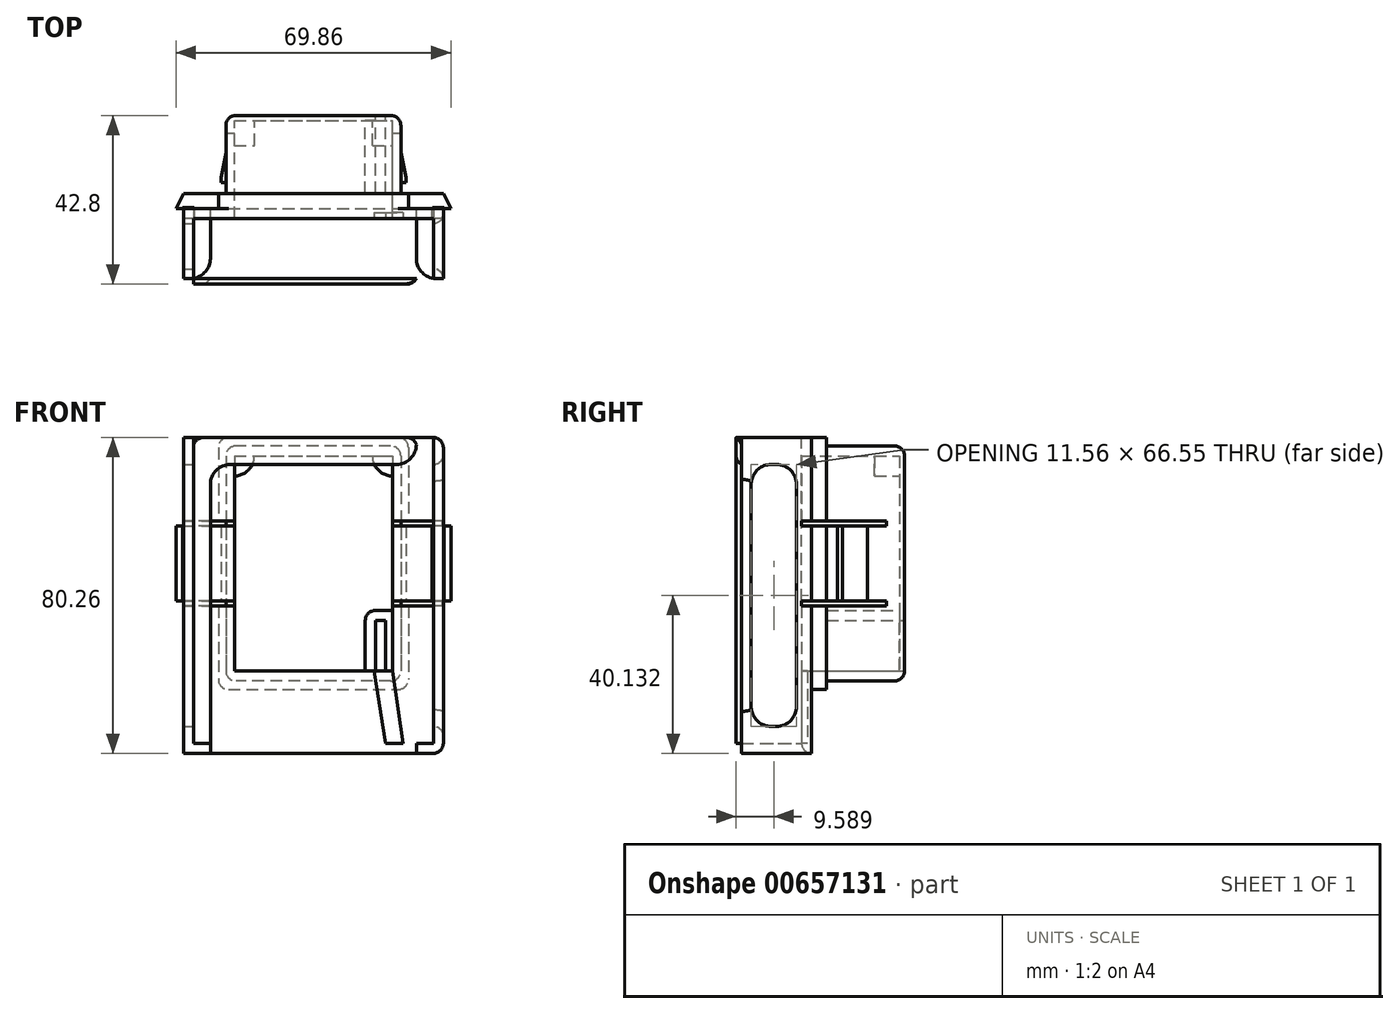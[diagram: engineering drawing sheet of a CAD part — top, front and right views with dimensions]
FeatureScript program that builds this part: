
annotation { "Feature Type Name" : "Feature", "Feature Type Description" : "" }
export const myFeature = defineFeature(function(context is Context, id is Id, definition is map)
    precondition{}
    {
        {
            var Q0;
            Q0=qCreatedBy(makeId("Front.planeOp"),FACE);
            var sketch = newSketch(context, id + "F0", { "sketchPlane" : qUnion([Q0])});
            skLineSegment(sketch, "E0.bottom", {"start": v(22.23, 29.85) * mm, "end": v(-22.23, 29.85) * mm});
            skLineSegment(sketch, "E0.top", {"start": v(22.22, -29.85) * mm, "end": v(-22.23, -29.85) * mm});
            skLineSegment(sketch, "E0.left", {"start": v(22.23, 29.84) * mm, "end": v(22.22, -29.85) * mm});
            skLineSegment(sketch, "E0.right", {"start": v(-22.23, 29.85) * mm, "end": v(-22.23, -29.85) * mm});
            skPoint(sketch, "E0.middle", {"position": v(0, 0) * mm});
            skLineSegment(sketch, "E1.bottom", {"start": v(-20.07, 27.3) * mm, "end": v(20.07, 27.3) * mm});
            skLineSegment(sketch, "E1.top", {"start": v(-20.07, -27.3) * mm, "end": v(13.2, -27.3) * mm});
            skLineSegment(sketch, "E1.left", {"start": v(-20.07, 27.3) * mm, "end": v(-20.07, -27.3) * mm});
            skLineSegment(sketch, "E1.right", {"start": v(20.07, 27.3) * mm, "end": v(20.07, -11.94) * mm});
            skLineSegment(sketch, "E2.bottom", {"start": v(15.75, -27.3) * mm, "end": v(18.42, -27.3) * mm});
            skLineSegment(sketch, "E2.top", {"start": v(15.75, -14.48) * mm, "end": v(18.42, -14.48) * mm});
            skLineSegment(sketch, "E2.left", {"start": v(15.75, -27.3) * mm, "end": v(15.75, -14.48) * mm});
            skLineSegment(sketch, "E2.right", {"start": v(18.42, -27.3) * mm, "end": v(18.42, -14.48) * mm});
            skLineSegment(sketch, "E3", {"start": v(13.2, -27.3) * mm, "end": v(13.2, -11.94) * mm});
            skLineSegment(sketch, "E4", {"start": v(13.2, -11.94) * mm, "end": v(20.07, -11.94) * mm});
            skPoint(sketch, "E5.orphan", {"position": v(20.07, -27.3) * mm});
            skSolve(sketch);
        }
        {
            var Q0;
            Q0=makeQuery(id+"F0.imprint","IMPRINT",FACE,{"disambiguationData":[TD([[makeQuery(id+"F0.imprint","IMPRINT",EDGE,{"derivedFrom":sQuery(id+"F0.wireOp",EDGE,"E0.bottom")}),1.0]])]});
            extrude(context, id + "F1", {"entities" : qUnion([Q0]), "depth" : 19.8 * mm, "offsetDistance" : 25.4 * mm});
        }
        {
            var Q0;
            Q0=makeQuery(id+"F0.imprint","IMPRINT",FACE,{"disambiguationData":[TD([[makeQuery(id+"F0.imprint","IMPRINT",EDGE,{"derivedFrom":sQuery(id+"F0.wireOp",EDGE,"E1.bottom")}),-1.0]])]});
            extrude(context, id + "F2", {"entities" : qUnion([Q0]), "operationType" : NewBodyOperationType.ADD, "depth" : 1.27 * mm, "offsetDistance" : 25.4 * mm});
        }
        {
            var Q0;
            Q0=makeQuery(id+"F2.opExtrude","CAP_FACE",FACE,{"disambiguationData":[OSD([sQuery(id+"F0.wireOp",EDGE,"E1.bottom"),sQuery(id+"F0.wireOp",EDGE,"E1.top"),sQuery(id+"F0.wireOp",EDGE,"E1.left"),sQuery(id+"F0.wireOp",EDGE,"E1.right"),sQuery(id+"F0.wireOp",EDGE,"E3"),sQuery(id+"F0.wireOp",EDGE,"E4")])],"isStart":false});
            var sketch = newSketch(context, id + "F3", { "sketchPlane" : qUnion([Q0])});
            skArc(sketch, "E6", {"start": v(-20.07, 22.23) * mm, "mid": v(-16.47, 23.71) * mm, "end": v(-14.99, 27.3) * mm});
            skArc(sketch, "E7", {"start": v(14.99, 27.3) * mm, "mid": v(16.47, 23.71) * mm, "end": v(20.07, 22.23) * mm});
            skSolve(sketch);
        }
        {
            var Q0;
            {var subQ0=sQuery(id+"F3.wireOp",EDGE,"E6");Q0=makeQuery(id+"F3.imprint","IMPRINT",FACE,{"disambiguationData":[TD([[makeQuery(id+"F3.imprint","IMPRINT",EDGE,{"derivedFrom":subQ0}),1.0]])]});}
            var Q1;
            {var subQ0=sQuery(id+"F3.wireOp",EDGE,"E7");Q1=makeQuery(id+"F3.imprint","IMPRINT",FACE,{"disambiguationData":[TD([[makeQuery(id+"F3.imprint","IMPRINT",EDGE,{"derivedFrom":subQ0}),1.0]])]});}
            extrude(context, id + "F4", {"entities" : qUnion([Q0, Q1]), "operationType" : NewBodyOperationType.ADD, "depth" : 6.35 * mm, "offsetDistance" : 25.4 * mm});
        }
        {
            var Q0;
            Q0=makeQuery(id+"F1.opExtrude","CAP_FACE",FACE,{"disambiguationData":[OSD([sQuery(id+"F0.wireOp",EDGE,"E0.bottom"),sQuery(id+"F0.wireOp",EDGE,"E0.top"),sQuery(id+"F0.wireOp",EDGE,"E0.left"),sQuery(id+"F0.wireOp",EDGE,"E0.right"),sQuery(id+"F0.wireOp",EDGE,"E1.bottom"),sQuery(id+"F0.wireOp",EDGE,"E1.top"),sQuery(id+"F0.wireOp",EDGE,"E1.left"),sQuery(id+"F0.wireOp",EDGE,"E1.right"),sQuery(id+"F0.wireOp",EDGE,"E2.top"),sQuery(id+"F0.wireOp",EDGE,"E2.left"),sQuery(id+"F0.wireOp",EDGE,"E2.right"),sQuery(id+"F0.wireOp",EDGE,"E3"),sQuery(id+"F0.wireOp",EDGE,"E4"),sQuery(id+"F0.wireOp",EDGE,"E2.bottom")])],"isStart":false});
            var sketch = newSketch(context, id + "F5", { "sketchPlane" : qUnion([Q0])});
            skLineSegment(sketch, "E8.bottom", {"start": v(-24.13, 32) * mm, "end": v(24.13, 32) * mm});
            skLineSegment(sketch, "E8.top", {"start": v(-24.13, -32) * mm, "end": v(24.13, -32) * mm});
            skLineSegment(sketch, "E8.left", {"start": v(-24.13, 32) * mm, "end": v(-24.13, -32) * mm});
            skLineSegment(sketch, "E8.right", {"start": v(24.13, 32) * mm, "end": v(24.13, -32) * mm});
            skPoint(sketch, "E8.middle", {"position": v(0, 0) * mm});
            skLineSegment(sketch, "E9.bottom", {"start": v(-20.07, 27.3) * mm, "end": v(20.07, 27.3) * mm});
            skLineSegment(sketch, "E9.top", {"start": v(-20.07, -27.3) * mm, "end": v(20.07, -27.3) * mm});
            skLineSegment(sketch, "E9.left", {"start": v(-20.07, 27.3) * mm, "end": v(-20.07, -27.3) * mm});
            skLineSegment(sketch, "E9.right", {"start": v(20.07, 27.3) * mm, "end": v(20.07, -27.3) * mm});
            skSolve(sketch);
        }
        {
            var Q0;
            Q0 = qSketchRegion(id + "F5", true);
            extrude(context, id + "F6", {"entities" : qUnion([Q0]), "operationType" : NewBodyOperationType.ADD, "depth" : 3.8 * mm, "offsetDistance" : 25.4 * mm});
        }
        {
            var Q0;
            Q0=makeQuery(id+"F6.opExtrude","CAP_FACE",FACE,{"disambiguationData":[OSD([sQuery(id+"F5.wireOp",EDGE,"E8.bottom"),sQuery(id+"F5.wireOp",EDGE,"E8.top"),sQuery(id+"F5.wireOp",EDGE,"E8.left"),sQuery(id+"F5.wireOp",EDGE,"E8.right"),sQuery(id+"F5.wireOp",EDGE,"E9.bottom"),sQuery(id+"F5.wireOp",EDGE,"E9.top"),sQuery(id+"F5.wireOp",EDGE,"E9.left"),sQuery(id+"F5.wireOp",EDGE,"E9.right")])],"isStart":false});
            var sketch = newSketch(context, id + "F7", { "sketchPlane" : qUnion([Q0])});
            skLineSegment(sketch, "E10.bottom", {"start": v(33.02, 32) * mm, "end": v(-33.02, 32) * mm});
            skLineSegment(sketch, "E10.top", {"start": v(33.02, -32) * mm, "end": v(-33.02, -32) * mm});
            skLineSegment(sketch, "E10.left", {"start": v(33.02, 32) * mm, "end": v(33.02, -48.26) * mm});
            skLineSegment(sketch, "E10.right", {"start": v(-33.02, 32) * mm, "end": v(-33.02, -48.26) * mm});
            skPoint(sketch, "E10.middle", {"position": v(0, 0) * mm});
            skLineSegment(sketch, "E11", {"start": v(-33.02, -48.26) * mm, "end": v(33.02, -48.26) * mm});
            skLineSegment(sketch, "E12", {"start": v(-30.48, 32) * mm, "end": v(-30.48, -45.72) * mm});
            skLineSegment(sketch, "E13", {"start": v(-30.48, -45.72) * mm, "end": v(30.48, -45.72) * mm});
            skLineSegment(sketch, "E14", {"start": v(30.48, -45.72) * mm, "end": v(30.48, 32) * mm});
            skLineSegment(sketch, "E15", {"start": v(-26.16, -45.72) * mm, "end": v(-26.16, -48.26) * mm});
            skLineSegment(sketch, "E16", {"start": v(26.16, -45.72) * mm, "end": v(26.16, -48.26) * mm});
            skSolve(sketch);
        }
        {
            var Q0;
            {var subQ2=makeQuery(id+"F6.opExtrude","CAP_EDGE",EDGE,{"disambiguationData":[OSD([sQuery(id+"F5.wireOp",EDGE,"E8.left")])],"isStart":false});Q0=makeQuery(id+"F7.imprint","IMPRINT",FACE,{"disambiguationData":[TD([[makeQuery(id+"F7.imprint","IMPRINT",EDGE,{"derivedFrom":subQ2}),1.0]])]});}
            var Q1;
            {var subQ1=makeQuery(id+"F6.opExtrude","CAP_EDGE",EDGE,{"disambiguationData":[OSD([sQuery(id+"F5.wireOp",EDGE,"E8.right")])],"isStart":false});Q1=makeQuery(id+"F7.imprint","IMPRINT",FACE,{"disambiguationData":[TD([[makeQuery(id+"F7.imprint","IMPRINT",EDGE,{"derivedFrom":subQ1}),1.0]])]});}
            var Q2;
            {var subQ1=makeQuery(id+"F6.opExtrude","CAP_EDGE",EDGE,{"disambiguationData":[OSD([sQuery(id+"F5.wireOp",EDGE,"E8.left")])],"isStart":false});Q2=makeQuery(id+"F7.imprint","IMPRINT",FACE,{"disambiguationData":[TD([[makeQuery(id+"F7.imprint","IMPRINT",EDGE,{"derivedFrom":subQ1}),-1.0]])]});}
            var Q3;
            {var subQ3=sQuery(id+"F7.wireOp",EDGE,"E10.top");var subQ6=makeQuery(id+"F7.imprint","INTERSECT",VERTEX,{"derivedFrom":[makeQuery(id+"F6.opExtrude","CAP_EDGE",EDGE,{"disambiguationData":[OSD([sQuery(id+"F5.wireOp",EDGE,"E8.right")])],"isStart":false}),subQ3]});var subQ8=sQuery(id+"F7.wireOp",EDGE,"E14");var subQ9=makeQuery(id+"F7.imprint","INTERSECT",VERTEX,{"derivedFrom":[subQ3,subQ8]});Q3=makeQuery(id+"F7.imprint","IMPRINT",FACE,{"disambiguationData":[TD([[makeQuery(id+"F7.imprint","IMPRINT",EDGE,{"disambiguationData":[TD([[subQ6,1.0],[subQ9,-1.0]])],"derivedFrom":subQ3}),1.0]])]});}
            var Q4;
            {var subQ0=sQuery(id+"F7.wireOp",EDGE,"E15");Q4=makeQuery(id+"F7.imprint","IMPRINT",FACE,{"disambiguationData":[TD([[makeQuery(id+"F7.imprint","IMPRINT",EDGE,{"derivedFrom":subQ0}),1.0]])]});}
            extrude(context, id + "F8", {"entities" : qUnion([Q0, Q1, Q2, Q3, Q4]), "operationType" : NewBodyOperationType.ADD, "depth" : 2.54 * mm, "offsetDistance" : 25.4 * mm});
        }
        {
            var Q0;
            {var subQ9=sQuery(id+"F7.wireOp",EDGE,"E15");Q0=makeQuery(id+"F7.imprint","IMPRINT",FACE,{"disambiguationData":[TD([[makeQuery(id+"F7.imprint","IMPRINT",EDGE,{"derivedFrom":subQ9}),-1.0]])]});}
            var Q1;
            {var subQ0=sQuery(id+"F7.wireOp",EDGE,"E10.right");var subQ1=sQuery(id+"F7.wireOp",EDGE,"E10.bottom");var subQ2=makeQuery(id+"F7.imprint","INTERSECT",VERTEX,{"derivedFrom":[subQ1,subQ0]});var subQ3=sQuery(id+"F7.wireOp",EDGE,"E12");var subQ4=makeQuery(id+"F7.imprint","INTERSECT",VERTEX,{"derivedFrom":[subQ1,subQ3]});Q1=makeQuery(id+"F7.imprint","IMPRINT",FACE,{"disambiguationData":[TD([[makeQuery(id+"F7.imprint","IMPRINT",EDGE,{"disambiguationData":[TD([[subQ2,1.0],[subQ4,-1.0]])],"derivedFrom":subQ1}),1.0]])]});}
            var Q2;
            {var subQ0=sQuery(id+"F7.wireOp",EDGE,"E10.left");var subQ1=sQuery(id+"F7.wireOp",EDGE,"E10.bottom");var subQ2=makeQuery(id+"F7.imprint","INTERSECT",VERTEX,{"derivedFrom":[subQ1,subQ0]});var subQ3=sQuery(id+"F7.wireOp",EDGE,"E14");var subQ4=makeQuery(id+"F7.imprint","INTERSECT",VERTEX,{"derivedFrom":[subQ1,subQ3]});Q2=makeQuery(id+"F7.imprint","IMPRINT",FACE,{"disambiguationData":[TD([[makeQuery(id+"F7.imprint","IMPRINT",EDGE,{"disambiguationData":[TD([[subQ2,-1.0],[subQ4,1.0]])],"derivedFrom":subQ1}),1.0]])]});}
            var Q3;
            {var subQ3=sQuery(id+"F7.wireOp",EDGE,"E16");Q3=makeQuery(id+"F7.imprint","IMPRINT",FACE,{"disambiguationData":[TD([[makeQuery(id+"F7.imprint","IMPRINT",EDGE,{"derivedFrom":subQ3}),1.0]])]});}
            extrude(context, id + "F9", {"entities" : qUnion([Q0, Q1, Q2, Q3]), "depth" : 17.78 * mm, "offsetDistance" : 25.4 * mm});
        }
        {
            var Q0;
            Q0=makeQuery(id+"F9.opExtrude","CAP_FACE",FACE,{"disambiguationData":[OSD([sQuery(id+"F7.wireOp",EDGE,"E10.bottom"),sQuery(id+"F7.wireOp",EDGE,"E10.right"),sQuery(id+"F7.wireOp",EDGE,"E11"),sQuery(id+"F7.wireOp",EDGE,"E12"),sQuery(id+"F7.wireOp",EDGE,"E13"),sQuery(id+"F7.wireOp",EDGE,"E15")])],"isStart":false});
            var sketch = newSketch(context, id + "F10", { "sketchPlane" : qUnion([Q0])});
            skLineSegment(sketch, "E17.0", {"start": v(-33.02, -48.26) * mm, "end": v(33.02, -48.26) * mm});
            skLineSegment(sketch, "E18.0", {"start": v(26.16, -45.72) * mm, "end": v(26.16, -48.26) * mm});
            skLineSegment(sketch, "E19.0", {"start": v(-26.16, -45.72) * mm, "end": v(-26.16, -48.26) * mm});
            skLineSegment(sketch, "E20.bottom", {"start": v(-26.16, -48.26) * mm, "end": v(-33.02, -48.26) * mm});
            skLineSegment(sketch, "E20.top", {"start": v(-26.16, 32) * mm, "end": v(-33.02, 32) * mm});
            skLineSegment(sketch, "E20.left", {"start": v(-26.16, -48.26) * mm, "end": v(-26.16, 32) * mm});
            skLineSegment(sketch, "E20.right", {"start": v(-33.02, -48.26) * mm, "end": v(-33.02, 32) * mm});
            skLineSegment(sketch, "E21.bottom", {"start": v(26.16, -48.26) * mm, "end": v(33.02, -48.26) * mm});
            skLineSegment(sketch, "E21.top", {"start": v(26.16, 32) * mm, "end": v(33.02, 32) * mm});
            skLineSegment(sketch, "E21.left", {"start": v(26.16, -48.26) * mm, "end": v(26.16, 32) * mm});
            skLineSegment(sketch, "E21.right", {"start": v(33.02, -48.26) * mm, "end": v(33.02, 32) * mm});
            skLineSegment(sketch, "E22.bottom", {"start": v(-26.16, -48.26) * mm, "end": v(26.16, -48.26) * mm});
            skLineSegment(sketch, "E22.top", {"start": v(-26.16, -41.4) * mm, "end": v(26.16, -41.4) * mm});
            skLineSegment(sketch, "E22.left", {"start": v(-26.16, -48.26) * mm, "end": v(-26.16, -41.4) * mm});
            skLineSegment(sketch, "E22.right", {"start": v(26.16, -48.26) * mm, "end": v(26.16, -41.4) * mm});
            skLineSegment(sketch, "E23.bottom", {"start": v(26.16, 32) * mm, "end": v(-26.16, 32) * mm});
            skLineSegment(sketch, "E23.top", {"start": v(26.16, 25.15) * mm, "end": v(-26.16, 25.15) * mm});
            skLineSegment(sketch, "E23.left", {"start": v(26.16, 32) * mm, "end": v(26.16, 25.15) * mm});
            skLineSegment(sketch, "E23.right", {"start": v(-26.16, 32) * mm, "end": v(-26.16, 25.15) * mm});
            skSolve(sketch);
        }
        {
            var Q0;
            {var subQ4=sQuery(id+"F10.wireOp",EDGE,"E20.bottom");Q0=makeQuery(id+"F10.imprint","IMPRINT",FACE,{"disambiguationData":[TD([[makeQuery(id+"F10.imprint","IMPRINT",EDGE,{"derivedFrom":subQ4}),1.0]])]});}
            var Q1;
            {var subQ4=sQuery(id+"F10.wireOp",EDGE,"E20.left");Q1=makeQuery(id+"F10.imprint","IMPRINT",FACE,{"disambiguationData":[TD([[makeQuery(id+"F10.imprint","IMPRINT",EDGE,{"derivedFrom":subQ4}),1.0]])]});}
            var Q2;
            Q2=makeQuery(id+"F10.imprint","IMPRINT",FACE,{"disambiguationData":[TD([[makeQuery(id+"F10.imprint","IMPRINT",EDGE,{"derivedFrom":sQuery(id+"F10.wireOp",EDGE,"E23.bottom")}),1.0]])]});
            var Q3;
            {var subQ1=sQuery(id+"F10.wireOp",EDGE,"E21.bottom");Q3=makeQuery(id+"F10.imprint","IMPRINT",FACE,{"disambiguationData":[TD([[makeQuery(id+"F10.imprint","IMPRINT",EDGE,{"derivedFrom":subQ1}),1.0]])]});}
            var Q4;
            {var subQ4=sQuery(id+"F10.wireOp",EDGE,"E22.bottom");Q4=makeQuery(id+"F10.imprint","IMPRINT",FACE,{"disambiguationData":[TD([[makeQuery(id+"F10.imprint","IMPRINT",EDGE,{"derivedFrom":subQ4}),1.0]])]});}
            extrude(context, id + "F11", {"entities" : qUnion([Q0, Q1, Q2, Q3, Q4]), "operationType" : NewBodyOperationType.ADD, "depth" : 1.4 * mm, "offsetDistance" : 25.4 * mm});
        }
        {
            var Q0;
            Q0=makeQuery(id+"F11.boolean.opBoolean","MERGE",FACE,{"derivedFrom":[makeQuery(id+"F9.opExtrude","SWEPT_FACE",FACE,{"disambiguationData":[OSD([sQuery(id+"F7.wireOp",EDGE,"E10.left")])]}),makeQuery(id+"F11.opExtrude","SWEPT_FACE",FACE,{"disambiguationData":[OSD([sQuery(id+"F10.wireOp",EDGE,"E21.right")])]})]});
            var sketch = newSketch(context, id + "F12", { "sketchPlane" : qUnion([Q0])});
            skLineSegment(sketch, "E24.bottom", {"start": v(-38.99, 25.15) * mm, "end": v(-27.43, 25.15) * mm});
            skLineSegment(sketch, "E24.top", {"start": v(-38.99, -41.4) * mm, "end": v(-27.43, -41.4) * mm});
            skLineSegment(sketch, "E24.left", {"start": v(-38.99, 25.15) * mm, "end": v(-38.99, -41.4) * mm});
            skLineSegment(sketch, "E24.right", {"start": v(-27.43, 25.15) * mm, "end": v(-27.43, -41.4) * mm});
            skSolve(sketch);
        }
        {
            var Q0;
            Q0=makeQuery(id+"F12.imprint","IMPRINT",FACE,{"disambiguationData":[TD([[makeQuery(id+"F12.imprint","IMPRINT",EDGE,{"derivedFrom":sQuery(id+"F12.wireOp",EDGE,"E24.bottom")}),-1.0]])]});
            extrude(context, id + "F13", {"entities" : qUnion([Q0]), "operationType" : NewBodyOperationType.REMOVE, "oppositeDirection" : true, "depth" : 76.2 * mm, "offsetDistance" : 25.4 * mm});
        }
        {
            var Q0;
            Q0=makeQuery(id+"F9.opExtrude","CAP_EDGE",EDGE,{"disambiguationData":[OSD([sQuery(id+"F7.wireOp",EDGE,"E15")])],"isStart":false});
            var Q1;
            Q1=makeQuery(id+"F9.opExtrude","CAP_EDGE",EDGE,{"disambiguationData":[OSD([sQuery(id+"F7.wireOp",EDGE,"E16")])],"isStart":false});
            var Q2;
            {var subQ0=sQuery(id+"F12.wireOp",EDGE,"E24.bottom");var subQ1=sQuery(id+"F12.wireOp",EDGE,"E24.left");Q2=makeQuery(id+"F13.boolean.opBoolean","COPY",EDGE,{"disambiguationData":[TD([makeQuery(id+"F9.opExtrude","SWEPT_FACE",FACE,{"disambiguationData":[OSD([sQuery(id+"F7.wireOp",EDGE,"E10.right")])]})])],"derivedFrom":makeQuery(id+"F13.opExtrude","SWEPT_EDGE",EDGE,{"disambiguationData":[OSD([subQ0,subQ1])]})});}
            var Q3;
            {var subQ0=sQuery(id+"F12.wireOp",EDGE,"E24.top");var subQ1=sQuery(id+"F12.wireOp",EDGE,"E24.left");Q3=makeQuery(id+"F13.boolean.opBoolean","COPY",EDGE,{"disambiguationData":[TD([makeQuery(id+"F9.opExtrude","SWEPT_FACE",FACE,{"disambiguationData":[OSD([sQuery(id+"F7.wireOp",EDGE,"E10.right")])]})])],"derivedFrom":makeQuery(id+"F13.opExtrude","SWEPT_EDGE",EDGE,{"disambiguationData":[OSD([subQ0,subQ1])]})});}
            var Q4;
            {var subQ0=sQuery(id+"F12.wireOp",EDGE,"E24.top");var subQ1=sQuery(id+"F12.wireOp",EDGE,"E24.right");Q4=makeQuery(id+"F13.boolean.opBoolean","COPY",EDGE,{"disambiguationData":[TD([makeQuery(id+"F9.opExtrude","SWEPT_FACE",FACE,{"disambiguationData":[OSD([sQuery(id+"F7.wireOp",EDGE,"E10.right")])]})])],"derivedFrom":makeQuery(id+"F13.opExtrude","SWEPT_EDGE",EDGE,{"disambiguationData":[OSD([subQ0,subQ1])]})});}
            var Q5;
            {var subQ0=sQuery(id+"F12.wireOp",EDGE,"E24.bottom");var subQ1=sQuery(id+"F12.wireOp",EDGE,"E24.right");Q5=makeQuery(id+"F13.boolean.opBoolean","COPY",EDGE,{"disambiguationData":[TD([makeQuery(id+"F9.opExtrude","SWEPT_FACE",FACE,{"disambiguationData":[OSD([sQuery(id+"F7.wireOp",EDGE,"E10.right")])]})])],"derivedFrom":makeQuery(id+"F13.opExtrude","SWEPT_EDGE",EDGE,{"disambiguationData":[OSD([subQ0,subQ1])]})});}
            var Q6;
            Q6=makeQuery(id+"F11.opExtrude","SWEPT_EDGE",EDGE,{"disambiguationData":[OSD([sQuery(id+"F10.wireOp",EDGE,"E20.left"),sQuery(id+"F10.wireOp",EDGE,"E23.top"),sQuery(id+"F10.wireOp",EDGE,"E23.right")])]});
            var Q7;
            Q7=makeQuery(id+"F11.opExtrude","SWEPT_EDGE",EDGE,{"disambiguationData":[OSD([sQuery(id+"F10.wireOp",EDGE,"E20.left"),sQuery(id+"F10.wireOp",EDGE,"E22.top"),sQuery(id+"F10.wireOp",EDGE,"E22.left")])]});
            var Q8;
            Q8=makeQuery(id+"F11.opExtrude","SWEPT_EDGE",EDGE,{"disambiguationData":[OSD([sQuery(id+"F10.wireOp",EDGE,"E21.left"),sQuery(id+"F10.wireOp",EDGE,"E23.top"),sQuery(id+"F10.wireOp",EDGE,"E23.left")])]});
            var Q9;
            Q9=makeQuery(id+"F11.opExtrude","SWEPT_EDGE",EDGE,{"disambiguationData":[OSD([sQuery(id+"F10.wireOp",EDGE,"E21.left"),sQuery(id+"F10.wireOp",EDGE,"E22.top"),sQuery(id+"F10.wireOp",EDGE,"E22.right")])]});
            var Q10;
            {var subQ0=sQuery(id+"F12.wireOp",EDGE,"E24.top");var subQ1=sQuery(id+"F12.wireOp",EDGE,"E24.left");Q10=makeQuery(id+"F13.boolean.opBoolean","COPY",EDGE,{"disambiguationData":[TD([makeQuery(id+"F9.opExtrude","SWEPT_FACE",FACE,{"disambiguationData":[OSD([sQuery(id+"F7.wireOp",EDGE,"E10.left")])]})])],"derivedFrom":makeQuery(id+"F13.opExtrude","SWEPT_EDGE",EDGE,{"disambiguationData":[OSD([subQ0,subQ1])]})});}
            var Q11;
            {var subQ0=sQuery(id+"F12.wireOp",EDGE,"E24.top");var subQ1=sQuery(id+"F12.wireOp",EDGE,"E24.right");Q11=makeQuery(id+"F13.boolean.opBoolean","COPY",EDGE,{"disambiguationData":[TD([makeQuery(id+"F9.opExtrude","SWEPT_FACE",FACE,{"disambiguationData":[OSD([sQuery(id+"F7.wireOp",EDGE,"E10.left")])]})])],"derivedFrom":makeQuery(id+"F13.opExtrude","SWEPT_EDGE",EDGE,{"disambiguationData":[OSD([subQ0,subQ1])]})});}
            var Q12;
            {var subQ0=sQuery(id+"F12.wireOp",EDGE,"E24.bottom");var subQ1=sQuery(id+"F12.wireOp",EDGE,"E24.left");Q12=makeQuery(id+"F13.boolean.opBoolean","COPY",EDGE,{"disambiguationData":[TD([makeQuery(id+"F9.opExtrude","SWEPT_FACE",FACE,{"disambiguationData":[OSD([sQuery(id+"F7.wireOp",EDGE,"E10.left")])]})])],"derivedFrom":makeQuery(id+"F13.opExtrude","SWEPT_EDGE",EDGE,{"disambiguationData":[OSD([subQ0,subQ1])]})});}
            var Q13;
            {var subQ0=sQuery(id+"F12.wireOp",EDGE,"E24.bottom");var subQ1=sQuery(id+"F12.wireOp",EDGE,"E24.right");Q13=makeQuery(id+"F13.boolean.opBoolean","COPY",EDGE,{"disambiguationData":[TD([makeQuery(id+"F9.opExtrude","SWEPT_FACE",FACE,{"disambiguationData":[OSD([sQuery(id+"F7.wireOp",EDGE,"E10.left")])]})])],"derivedFrom":makeQuery(id+"F13.opExtrude","SWEPT_EDGE",EDGE,{"disambiguationData":[OSD([subQ0,subQ1])]})});}
            fillet(context, id + "F14", {"entities" : qUnion([Q0, Q1, Q2, Q3, Q4, Q5, Q6, Q7, Q8, Q9, Q10, Q11, Q12, Q13]), "radius" : 5.08 * mm, "tangentPropagation" : true, "allowEdgeOverflow" : false});
        }
        {
            var Q0;
            Q0=makeQuery(id+"F11.boolean.opBoolean","MERGE",EDGE,{"derivedFrom":[makeQuery(id+"F9.opExtrude","SWEPT_EDGE",EDGE,{"disambiguationData":[OSD([sQuery(id+"F7.wireOp",EDGE,"E10.right"),sQuery(id+"F7.wireOp",EDGE,"E11")])]}),makeQuery(id+"F11.opExtrude","SWEPT_EDGE",EDGE,{"disambiguationData":[OSD([sQuery(id+"F10.wireOp",EDGE,"E20.bottom"),sQuery(id+"F10.wireOp",EDGE,"E20.right")])]})]});
            var Q1;
            Q1=makeQuery(id+"F11.opExtrude","CAP_EDGE",EDGE,{"disambiguationData":[OSD([sQuery(id+"F10.wireOp",EDGE,"E20.right")])],"isStart":false});
            var Q2;
            Q2=makeQuery(id+"F13.boolean.opBoolean","INTERSECT",EDGE,{"derivedFrom":[makeQuery(id+"F11.boolean.opBoolean","MERGE",FACE,{"derivedFrom":[makeQuery(id+"F9.opExtrude","SWEPT_FACE",FACE,{"disambiguationData":[OSD([sQuery(id+"F7.wireOp",EDGE,"E10.right")])]}),makeQuery(id+"F11.opExtrude","SWEPT_FACE",FACE,{"disambiguationData":[OSD([sQuery(id+"F10.wireOp",EDGE,"E20.right")])]})]}),makeQuery(id+"F13.opExtrude","SWEPT_FACE",FACE,{"disambiguationData":[OSD([sQuery(id+"F12.wireOp",EDGE,"E24.right")])]})]});
            var Q3;
            Q3=makeQuery(id+"F11.opExtrude","CAP_EDGE",EDGE,{"disambiguationData":[OSD([sQuery(id+"F10.wireOp",EDGE,"E20.left")])],"isStart":false});
            var Q4;
            Q4=makeQuery(id+"F11.opExtrude","CAP_EDGE",EDGE,{"disambiguationData":[OSD([sQuery(id+"F10.wireOp",EDGE,"E21.right")])],"isStart":false});
            var Q5;
            {var subQ0=makeQuery(id+"F11.opExtrude","SWEPT_FACE",FACE,{"disambiguationData":[OSD([sQuery(id+"F10.wireOp",EDGE,"E21.right")])]});var subQ1=makeQuery(id+"F9.opExtrude","SWEPT_FACE",FACE,{"disambiguationData":[OSD([sQuery(id+"F7.wireOp",EDGE,"E10.left")])]});var subQ2=sQuery(id+"F12.wireOp",EDGE,"E24.bottom");var subQ3=sQuery(id+"F12.wireOp",EDGE,"E24.right");Q5=makeQuery(id+"F14.opFillet","BLEND_EDGE",EDGE,{"blendedFrom":[makeQuery(id+"F13.boolean.opBoolean","COPY",EDGE,{"disambiguationData":[TD([subQ1])],"derivedFrom":makeQuery(id+"F13.opExtrude","SWEPT_EDGE",EDGE,{"disambiguationData":[OSD([subQ2,subQ3])]})}),makeQuery(id+"F11.boolean.opBoolean","MERGE",FACE,{"derivedFrom":[subQ1,subQ0]})],"blendedInto":[makeQuery(id+"F11.boolean.opBoolean","MERGE",FACE,{"derivedFrom":[subQ1,subQ0]})]});}
            var Q6;
            Q6=makeQuery(id+"F11.boolean.opBoolean","MERGE",EDGE,{"derivedFrom":[makeQuery(id+"F9.opExtrude","SWEPT_EDGE",EDGE,{"disambiguationData":[OSD([sQuery(id+"F7.wireOp",EDGE,"E10.bottom"),sQuery(id+"F7.wireOp",EDGE,"E10.left")])]}),makeQuery(id+"F11.opExtrude","SWEPT_EDGE",EDGE,{"disambiguationData":[OSD([sQuery(id+"F10.wireOp",EDGE,"E21.top"),sQuery(id+"F10.wireOp",EDGE,"E21.right")])]})]});
            var Q7;
            Q7=makeQuery(id+"F11.boolean.opBoolean","MERGE",EDGE,{"derivedFrom":[makeQuery(id+"F9.opExtrude","SWEPT_EDGE",EDGE,{"disambiguationData":[OSD([sQuery(id+"F7.wireOp",EDGE,"E10.left"),sQuery(id+"F7.wireOp",EDGE,"E11")])]}),makeQuery(id+"F11.opExtrude","SWEPT_EDGE",EDGE,{"disambiguationData":[OSD([sQuery(id+"F10.wireOp",EDGE,"E21.bottom"),sQuery(id+"F10.wireOp",EDGE,"E21.right")])]})]});
            var Q8;
            Q8=makeQuery(id+"F11.opExtrude","CAP_EDGE",EDGE,{"disambiguationData":[OSD([sQuery(id+"F10.wireOp",EDGE,"E20.bottom"),sQuery(id+"F10.wireOp",EDGE,"E21.bottom"),sQuery(id+"F10.wireOp",EDGE,"E22.bottom")])],"isStart":false});
            var Q9;
            Q9=makeQuery(id+"F9.opExtrude","SWEPT_EDGE",EDGE,{"disambiguationData":[OSD([sQuery(id+"F7.wireOp",EDGE,"E11"),sQuery(id+"F7.wireOp",EDGE,"E15")])]});
            var Q10;
            Q10=makeQuery(id+"F11.boolean.opBoolean","MERGE",EDGE,{"derivedFrom":[makeQuery(id+"F9.opExtrude","SWEPT_EDGE",EDGE,{"disambiguationData":[OSD([sQuery(id+"F7.wireOp",EDGE,"E10.bottom"),sQuery(id+"F7.wireOp",EDGE,"E10.right")])]}),makeQuery(id+"F11.opExtrude","SWEPT_EDGE",EDGE,{"disambiguationData":[OSD([sQuery(id+"F10.wireOp",EDGE,"E20.top"),sQuery(id+"F10.wireOp",EDGE,"E20.right")])]})]});
            var Q11;
            Q11=makeQuery(id+"F8.opExtrude","CAP_EDGE",EDGE,{"disambiguationData":[OSD([sQuery(id+"F7.wireOp",EDGE,"E11")])],"isStart":false});
            var Q12;
            Q12=makeQuery(id+"F1.opExtrude","SWEPT_EDGE",EDGE,{"disambiguationData":[OSD([sQuery(id+"F0.wireOp",EDGE,"E3"),sQuery(id+"F0.wireOp",EDGE,"E4")])]});
            var Q13;
            Q13=makeQuery(id+"F1.opExtrude","SWEPT_EDGE",EDGE,{"disambiguationData":[OSD([sQuery(id+"F0.wireOp",EDGE,"E0.top"),sQuery(id+"F0.wireOp",EDGE,"E0.right")])]});
            var Q14;
            Q14=makeQuery(id+"F1.opExtrude","SWEPT_EDGE",EDGE,{"disambiguationData":[OSD([sQuery(id+"F0.wireOp",EDGE,"E0.top"),sQuery(id+"F0.wireOp",EDGE,"E0.left")])]});
            var Q15;
            Q15=makeQuery(id+"F1.opExtrude","SWEPT_EDGE",EDGE,{"disambiguationData":[OSD([sQuery(id+"F0.wireOp",EDGE,"E0.bottom"),sQuery(id+"F0.wireOp",EDGE,"E0.left")])]});
            var Q16;
            Q16=makeQuery(id+"F1.opExtrude","SWEPT_EDGE",EDGE,{"disambiguationData":[OSD([sQuery(id+"F0.wireOp",EDGE,"E0.bottom"),sQuery(id+"F0.wireOp",EDGE,"E0.right")])]});
            var Q17;
            Q17=makeQuery(id+"F1.opExtrude","CAP_EDGE",EDGE,{"disambiguationData":[OSD([sQuery(id+"F0.wireOp",EDGE,"E0.top")])],"isStart":true});
            var Q18;
            Q18=makeQuery(id+"F1.opExtrude","CAP_EDGE",EDGE,{"disambiguationData":[OSD([sQuery(id+"F0.wireOp",EDGE,"E0.left")])],"isStart":true});
            var Q19;
            Q19=makeQuery(id+"F1.opExtrude","CAP_EDGE",EDGE,{"disambiguationData":[OSD([sQuery(id+"F0.wireOp",EDGE,"E0.right")])],"isStart":true});
            var Q20;
            Q20=makeQuery(id+"F1.opExtrude","CAP_EDGE",EDGE,{"disambiguationData":[OSD([sQuery(id+"F0.wireOp",EDGE,"E0.bottom")])],"isStart":true});
            var Q21;
            Q21=makeQuery(id+"F6.opExtrude","SWEPT_EDGE",EDGE,{"disambiguationData":[OSD([sQuery(id+"F5.wireOp",EDGE,"E8.top"),sQuery(id+"F5.wireOp",EDGE,"E8.right")])]});
            var Q22;
            Q22=makeQuery(id+"F6.opExtrude","SWEPT_EDGE",EDGE,{"disambiguationData":[OSD([sQuery(id+"F5.wireOp",EDGE,"E8.bottom"),sQuery(id+"F5.wireOp",EDGE,"E8.right")])]});
            var Q23;
            Q23=makeQuery(id+"F6.opExtrude","SWEPT_EDGE",EDGE,{"disambiguationData":[OSD([sQuery(id+"F5.wireOp",EDGE,"E8.bottom"),sQuery(id+"F5.wireOp",EDGE,"E8.left")])]});
            var Q24;
            Q24=makeQuery(id+"F6.opExtrude","SWEPT_EDGE",EDGE,{"disambiguationData":[OSD([sQuery(id+"F5.wireOp",EDGE,"E8.top"),sQuery(id+"F5.wireOp",EDGE,"E8.left")])]});
            fillet(context, id + "F15", {"entities" : qUnion([Q0, Q1, Q2, Q3, Q4, Q5, Q6, Q7, Q8, Q9, Q10, Q11, Q12, Q13, Q14, Q15, Q16, Q17, Q18, Q19, Q20, Q21, Q22, Q23, Q24]), "radius" : 2.54 * mm, "tangentPropagation" : true, "allowEdgeOverflow" : false});
        }
        {
            var Q0;
            Q0=qCreatedBy(makeId("Top.planeOp"),FACE);
            var sketch = newSketch(context, id + "F16", { "sketchPlane" : qUnion([Q0])});
            skLineSegment(sketch, "E25.0", {"start": v(22.23, -19.81) * mm, "end": v(22.23, -2.54) * mm});
            skPoint(sketch, "E25.1", {"position": v(22.23, -11.18) * mm});
            skLineSegment(sketch, "E26", {"start": v(22.23, -17.02) * mm, "end": v(23.5, -17.02) * mm});
            skLineSegment(sketch, "E27", {"start": v(23.5, -17.02) * mm, "end": v(23.5, -15.75) * mm});
            skLineSegment(sketch, "E28", {"start": v(23.5, -15.75) * mm, "end": v(22.23, -9.4) * mm});
            skLineSegment(sketch, "E29", {"start": v(0, 0) * mm, "end": v(0, -37.97) * mm, "construction": true});
            skLineSegment(sketch, "E30.MirrorCS", {"start": v(-22.23, -19.81) * mm, "end": v(-22.23, -2.54) * mm});
            skLineSegment(sketch, "E31.MirrorCS", {"start": v(-22.23, -17.02) * mm, "end": v(-23.5, -17.02) * mm});
            skLineSegment(sketch, "E32.MirrorCS", {"start": v(-23.5, -17.02) * mm, "end": v(-23.5, -15.75) * mm});
            skLineSegment(sketch, "E33.MirrorCS", {"start": v(-23.5, -15.75) * mm, "end": v(-22.23, -9.4) * mm});
            skSolve(sketch);
        }
        {
            var Q0;
            {var subQ0=sQuery(id+"F16.wireOp",EDGE,"E31.MirrorCS");Q0=makeQuery(id+"F16.imprint","IMPRINT",FACE,{"disambiguationData":[TD([[makeQuery(id+"F16.imprint","IMPRINT",EDGE,{"derivedFrom":subQ0}),-1.0]])]});}
            var Q1;
            {var subQ0=sQuery(id+"F16.wireOp",EDGE,"E26");Q1=makeQuery(id+"F16.imprint","IMPRINT",FACE,{"disambiguationData":[TD([[makeQuery(id+"F16.imprint","IMPRINT",EDGE,{"derivedFrom":subQ0}),1.0]])]});}
            extrude(context, id + "F17", {"entities" : qUnion([Q0, Q1]), "operationType" : NewBodyOperationType.ADD, "depth" : 19.05 * mm, "offsetDistance" : 25.4 * mm, "symmetric" : true});
        }
        {
            var Q0;
            Q0=makeQuery(id+"F1.opExtrude","SWEPT_FACE",FACE,{"disambiguationData":[OSD([sQuery(id+"F0.wireOp",EDGE,"E0.right")])]});
            var sketch = newSketch(context, id + "F18", { "sketchPlane" : qUnion([Q0])});
            skLineSegment(sketch, "E34.0", {"start": v(26.16, 32) * mm, "end": v(26.16, -45.72) * mm});
            skLineSegment(sketch, "E35.bottom", {"start": v(4.57, 9.52) * mm, "end": v(26.16, 9.52) * mm});
            skLineSegment(sketch, "E35.top", {"start": v(4.57, 10.8) * mm, "end": v(26.16, 10.8) * mm});
            skLineSegment(sketch, "E35.left", {"start": v(4.57, 9.52) * mm, "end": v(4.57, 10.8) * mm});
            skLineSegment(sketch, "E35.right", {"start": v(26.16, 9.52) * mm, "end": v(26.16, 10.8) * mm});
            skLineSegment(sketch, "E36", {"start": v(0, 0) * mm, "end": v(30.4, 0) * mm, "construction": true});
            skLineSegment(sketch, "E37.MirrorCS", {"start": v(4.57, -9.52) * mm, "end": v(26.16, -9.52) * mm});
            skLineSegment(sketch, "E38.MirrorCS", {"start": v(4.57, -10.8) * mm, "end": v(26.16, -10.8) * mm});
            skLineSegment(sketch, "E39.MirrorCS", {"start": v(4.57, -9.52) * mm, "end": v(4.57, -10.8) * mm});
            skLineSegment(sketch, "E40.MirrorCS", {"start": v(26.16, -32) * mm, "end": v(26.16, 45.72) * mm});
            skSolve(sketch);
        }
        {
            var Q0;
            Q0 = qSketchRegion(id + "F18", true);
            extrude(context, id + "F19", {"entities" : qUnion([Q0]), "operationType" : NewBodyOperationType.REMOVE, "oppositeDirection" : true, "depth" : 127 * mm, "offsetDistance" : 25.4 * mm, "symmetric" : true});
        }
        {
            var Q0;
            {var subQ8=sQuery(id+"F5.wireOp",EDGE,"E8.left");Q0=makeQuery(id+"F19.boolean.opBoolean","SPLIT",FACE,{"disambiguationData":[TD([makeQuery(id+"F19.opExtrude","SWEPT_FACE",FACE,{"disambiguationData":[OSD([sQuery(id+"F18.wireOp",EDGE,"E35.bottom")])]})])],"derivedFrom":makeQuery(id+"F6.opExtrude","SWEPT_FACE",FACE,{"disambiguationData":[OSD([subQ8])]})});}
            var sketch = newSketch(context, id + "F20", { "sketchPlane" : qUnion([Q0])});
            skLineSegment(sketch, "E41.bottom", {"start": v(23.62, 9.52) * mm, "end": v(19.81, 9.52) * mm});
            skLineSegment(sketch, "E41.top", {"start": v(23.62, -9.53) * mm, "end": v(19.81, -9.53) * mm});
            skLineSegment(sketch, "E41.left", {"start": v(23.62, 9.52) * mm, "end": v(23.62, -9.53) * mm});
            skLineSegment(sketch, "E41.right", {"start": v(19.81, 9.52) * mm, "end": v(19.81, -9.53) * mm});
            skSolve(sketch);
        }
        {
            var Q0;
            Q0 = qSketchRegion(id + "F20", true);
            extrude(context, id + "F21", {"entities" : qUnion([Q0]), "operationType" : NewBodyOperationType.ADD, "depth" : 11.43 * mm, "offsetDistance" : 25.4 * mm});
        }
        {
            var Q0;
            Q0=makeQuery(id+"F21.opExtrude","CAP_EDGE",EDGE,{"disambiguationData":[OSD([sQuery(id+"F20.wireOp",EDGE,"E41.right")])],"isStart":false});
            chamfer(context, id + "F22", {"entities" : qUnion([Q0]), "chamferType" : ChamferType.TWO_OFFSETS, "width1" : 5.08 * mm, "oppositeDirection" : false, "width2" : 2.54 * mm, "tangentPropagation" : true});
        }
        {
            var Q0;
            {var subQ8=sQuery(id+"F5.wireOp",EDGE,"E8.right");Q0=makeQuery(id+"F19.boolean.opBoolean","SPLIT",FACE,{"disambiguationData":[TD([makeQuery(id+"F19.opExtrude","SWEPT_FACE",FACE,{"disambiguationData":[OSD([sQuery(id+"F18.wireOp",EDGE,"E35.bottom")])]})])],"derivedFrom":makeQuery(id+"F6.opExtrude","SWEPT_FACE",FACE,{"disambiguationData":[OSD([subQ8])]})});}
            var sketch = newSketch(context, id + "F23", { "sketchPlane" : qUnion([Q0])});
            skLineSegment(sketch, "E42.bottom", {"start": v(-23.62, 9.53) * mm, "end": v(-19.81, 9.53) * mm});
            skLineSegment(sketch, "E42.top", {"start": v(-23.62, -9.52) * mm, "end": v(-19.81, -9.52) * mm});
            skLineSegment(sketch, "E42.left", {"start": v(-23.62, 9.53) * mm, "end": v(-23.62, -9.52) * mm});
            skLineSegment(sketch, "E42.right", {"start": v(-19.81, 9.53) * mm, "end": v(-19.81, -9.52) * mm});
            skSolve(sketch);
        }
        {
            var Q0;
            Q0=makeQuery(id+"F23.imprint","IMPRINT",FACE,{"disambiguationData":[TD([[makeQuery(id+"F23.imprint","IMPRINT",EDGE,{"derivedFrom":sQuery(id+"F23.wireOp",EDGE,"E42.bottom")}),-1.0]])]});
            extrude(context, id + "F24", {"entities" : qUnion([Q0]), "operationType" : NewBodyOperationType.ADD, "depth" : 11.43 * mm, "offsetDistance" : 25.4 * mm});
        }
        {
            var Q0;
            Q0=makeQuery(id+"F24.opExtrude","CAP_EDGE",EDGE,{"disambiguationData":[OSD([sQuery(id+"F23.wireOp",EDGE,"E42.right")])],"isStart":false});
            chamfer(context, id + "F25", {"entities" : qUnion([Q0]), "chamferType" : ChamferType.TWO_OFFSETS, "width1" : 2.54 * mm, "oppositeDirection" : false, "width2" : 5.08 * mm, "tangentPropagation" : true});
        }
        {
            var Q0;
            {var subQ0=sQuery(id+"F7.wireOp",EDGE,"E14");var subQ1=sQuery(id+"F7.wireOp",EDGE,"E13");var subQ2=sQuery(id+"F7.wireOp",EDGE,"E16");var subQ3=sQuery(id+"F7.wireOp",EDGE,"E12");var subQ4=sQuery(id+"F7.wireOp",EDGE,"E15");var subQ5=sQuery(id+"F5.wireOp",EDGE,"E9.right");var subQ6=sQuery(id+"F7.wireOp",EDGE,"E11");var subQ7=sQuery(id+"F5.wireOp",EDGE,"E9.left");var subQ8=sQuery(id+"F5.wireOp",EDGE,"E9.top");Q0=makeQuery(id+"F19.boolean.opBoolean","SPLIT",FACE,{"disambiguationData":[TD([makeQuery(id+"F1.opExtrude","SWEPT_FACE",FACE,{"disambiguationData":[OSD([sQuery(id+"F0.wireOp",EDGE,"E1.top")])]})])],"derivedFrom":makeQuery(id+"F8.opExtrude","CAP_FACE",FACE,{"disambiguationData":[OSD([sQuery(id+"F5.wireOp",EDGE,"E9.bottom"),subQ8,subQ7,subQ5,sQuery(id+"F7.wireOp",EDGE,"E10.bottom"),subQ6,subQ3,subQ1,subQ0,subQ4,subQ2])],"isStart":false})});}
            var sketch = newSketch(context, id + "F26", { "sketchPlane" : qUnion([Q0])});
            skLineSegment(sketch, "E43", {"start": v(20.07, -27.3) * mm, "end": v(15.5, -27.3) * mm});
            skLineSegment(sketch, "E44", {"start": v(15.5, -27.3) * mm, "end": v(18.67, -48.26) * mm});
            skLineSegment(sketch, "E45", {"start": v(23.25, -48.26) * mm, "end": v(20.07, -27.3) * mm});
            skLineSegment(sketch, "E46.0", {"start": v(-33.02, -48.26) * mm, "end": v(17.15, -48.26) * mm});
            skLineSegment(sketch, "E47", {"start": v(17.15, -48.26) * mm, "end": v(24.56, -48.26) * mm});
            skPoint(sketch, "E48.orphan", {"position": v(22.86, -45.72) * mm});
            skLineSegment(sketch, "E49.trimOffspring", {"start": v(18.67, -48.26) * mm, "end": v(23.25, -48.26) * mm});
            skLineSegment(sketch, "E50.trimOffspring", {"start": v(24.56, -48.26) * mm, "end": v(33.02, -48.26) * mm});
            skSolve(sketch);
        }
        {
            var Q0;
            Q0=makeQuery(id+"F26.imprint","IMPRINT",FACE,{"disambiguationData":[TD([[makeQuery(id+"F26.imprint","IMPRINT",EDGE,{"derivedFrom":sQuery(id+"F26.wireOp",EDGE,"E43")}),-1.0]])]});
            var Q1;
            {var subQ0=sQuery(id+"F26.wireOp",EDGE,"E49.trimOffspring");Q1=makeQuery(id+"F26.imprint","IMPRINT",FACE,{"disambiguationData":[TD([[makeQuery(id+"F26.imprint","IMPRINT",EDGE,{"derivedFrom":subQ0}),1.0]])]});}
            extrude(context, id + "F27", {"entities" : qUnion([Q0, Q1]), "operationType" : NewBodyOperationType.REMOVE, "oppositeDirection" : true, "depth" : 1.52 * mm, "offsetDistance" : 25.4 * mm});
        }
        {
            var Q0;
            Q0=makeQuery(id+"F21.boolean.opBoolean","MERGE",FACE,{"derivedFrom":[makeQuery(id+"F19.boolean.opBoolean","MERGE",FACE,{"derivedFrom":[makeQuery(id+"F17.opExtrude","CAP_FACE",FACE,{"disambiguationData":[OSD([sQuery(id+"F16.wireOp",EDGE,"E30.MirrorCS"),sQuery(id+"F16.wireOp",EDGE,"E31.MirrorCS"),sQuery(id+"F16.wireOp",EDGE,"E32.MirrorCS"),sQuery(id+"F16.wireOp",EDGE,"E33.MirrorCS")])],"isStart":false}),makeQuery(id+"F19.opExtrude","SWEPT_FACE",FACE,{"disambiguationData":[OSD([sQuery(id+"F18.wireOp",EDGE,"E35.bottom")])]})]}),makeQuery(id+"F21.opExtrude","SWEPT_FACE",FACE,{"disambiguationData":[OSD([sQuery(id+"F20.wireOp",EDGE,"E41.bottom")])]})]});
            var sketch = newSketch(context, id + "F28", { "sketchPlane" : qUnion([Q0])});
            skLineSegment(sketch, "E51", {"start": v(-30.48, -26.16) * mm, "end": v(-30.23, -26.16) * mm});
            skLineSegment(sketch, "E52", {"start": v(-30.23, -26.16) * mm, "end": v(-30.23, -23.62) * mm});
            skLineSegment(sketch, "E53", {"start": v(-30.48, -23.37) * mm, "end": v(-33.27, -23.37) * mm});
            skLineSegment(sketch, "E54", {"start": v(-33.27, -23.37) * mm, "end": v(-33.27, -23.62) * mm});
            skLineSegment(sketch, "E55", {"start": v(-33.27, -23.62) * mm, "end": v(-30.48, -23.62) * mm});
            skLineSegment(sketch, "E56", {"start": v(-30.48, -23.62) * mm, "end": v(-30.48, -26.16) * mm});
            skPoint(sketch, "E57.visualSharp", {"position": v(-30.23, -23.37) * mm});
            skArc(sketch, "E57.filletArc", {"start": v(-30.23, -23.62) * mm, "mid": v(-30.3, -23.44) * mm, "end": v(-30.48, -23.37) * mm});
            skLineSegment(sketch, "E58.MirrorCS", {"start": v(30.23, -26.16) * mm, "end": v(30.23, -23.62) * mm});
            skLineSegment(sketch, "E59.MirrorCS", {"start": v(30.48, -23.62) * mm, "end": v(30.48, -26.16) * mm});
            skArc(sketch, "E60.MirrorCS", {"start": v(30.23, -23.62) * mm, "mid": v(30.3, -23.44) * mm, "end": v(30.48, -23.37) * mm});
            skLineSegment(sketch, "E61.MirrorCS", {"start": v(30.48, -23.37) * mm, "end": v(33.27, -23.37) * mm});
            skLineSegment(sketch, "E62.MirrorCS", {"start": v(33.27, -23.62) * mm, "end": v(30.48, -23.62) * mm});
            skLineSegment(sketch, "E63.MirrorCS", {"start": v(30.48, -26.16) * mm, "end": v(30.23, -26.16) * mm});
            skLineSegment(sketch, "E64.MirrorCS", {"start": v(33.27, -23.37) * mm, "end": v(33.27, -23.62) * mm});
            skSolve(sketch);
        }
        {
            var Q0;
            Q0 = qSketchRegion(id + "F28", true);
            extrude(context, id + "F29", {"entities" : qUnion([Q0]), "operationType" : NewBodyOperationType.REMOVE, "oppositeDirection" : true, "depth" : 19.05 * mm, "offsetDistance" : 25.4 * mm});
        }
    });
